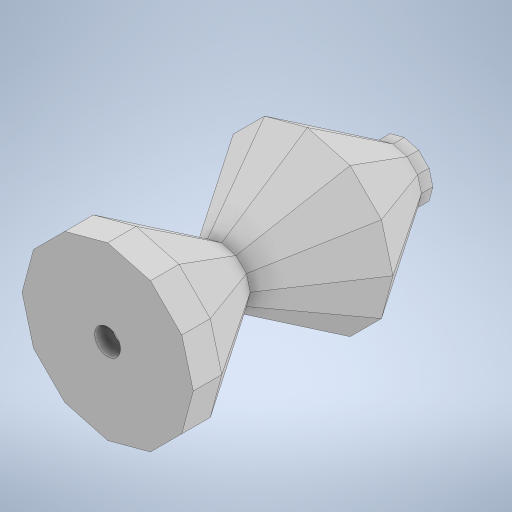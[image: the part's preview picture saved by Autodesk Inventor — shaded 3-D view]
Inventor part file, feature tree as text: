
AUTODESK INVENTOR PART (.ipt)
format: ipt  version: 2023 (Build 270158000, 158)  size: 351,744 bytes
history: native  units: in
note: dims shown in document units (in); Inventor stores cm internally (conversion verified against a paired STEP export)
features: sketch x6, extrude x4, projected_geometry x3, other x2, mirror x2, loft x1, shell x1
ambient origin geometry x8: Origin, YZ Plane, XZ Plane, XY Plane, X Axis, Y Axis, Z Axis, Center Point
bodies: Body1 (feature_tree)
feature tree (19):
  other  "솔리드1"
  sketch  "스케치1"
  other  "작업 평면1"
  loft  "로프트1"
  mirror  "미러1"
  mirror  "미러2"
  extrude  "돌출1"  Depth=0.5906in
  shell  "쉘1"  Thickness=0.3937in
  extrude  "돌출2"  TaperAngle=0.0deg  [1 undecoded]
  extrude  "돌출3"  TaperAngle=0.0deg  [1 undecoded]
  extrude  "돌출4"  Depth=0.0984in TaperAngle=0.0deg
  sketch  "스케치2"
  sketch  "스케치3"
  projected_geometry  "투영된 루프1"
  sketch  "스케치4"
  projected_geometry  "투영된 루프2"
  sketch  "스케치5"
  sketch  "스케치6"
  projected_geometry  "투영된 루프3"
note: 2 required parameter values undecoded (feature->parameter linkage not recoverable at this tier; creation-order binding heuristic only, values carry confidence <= 0.55)
